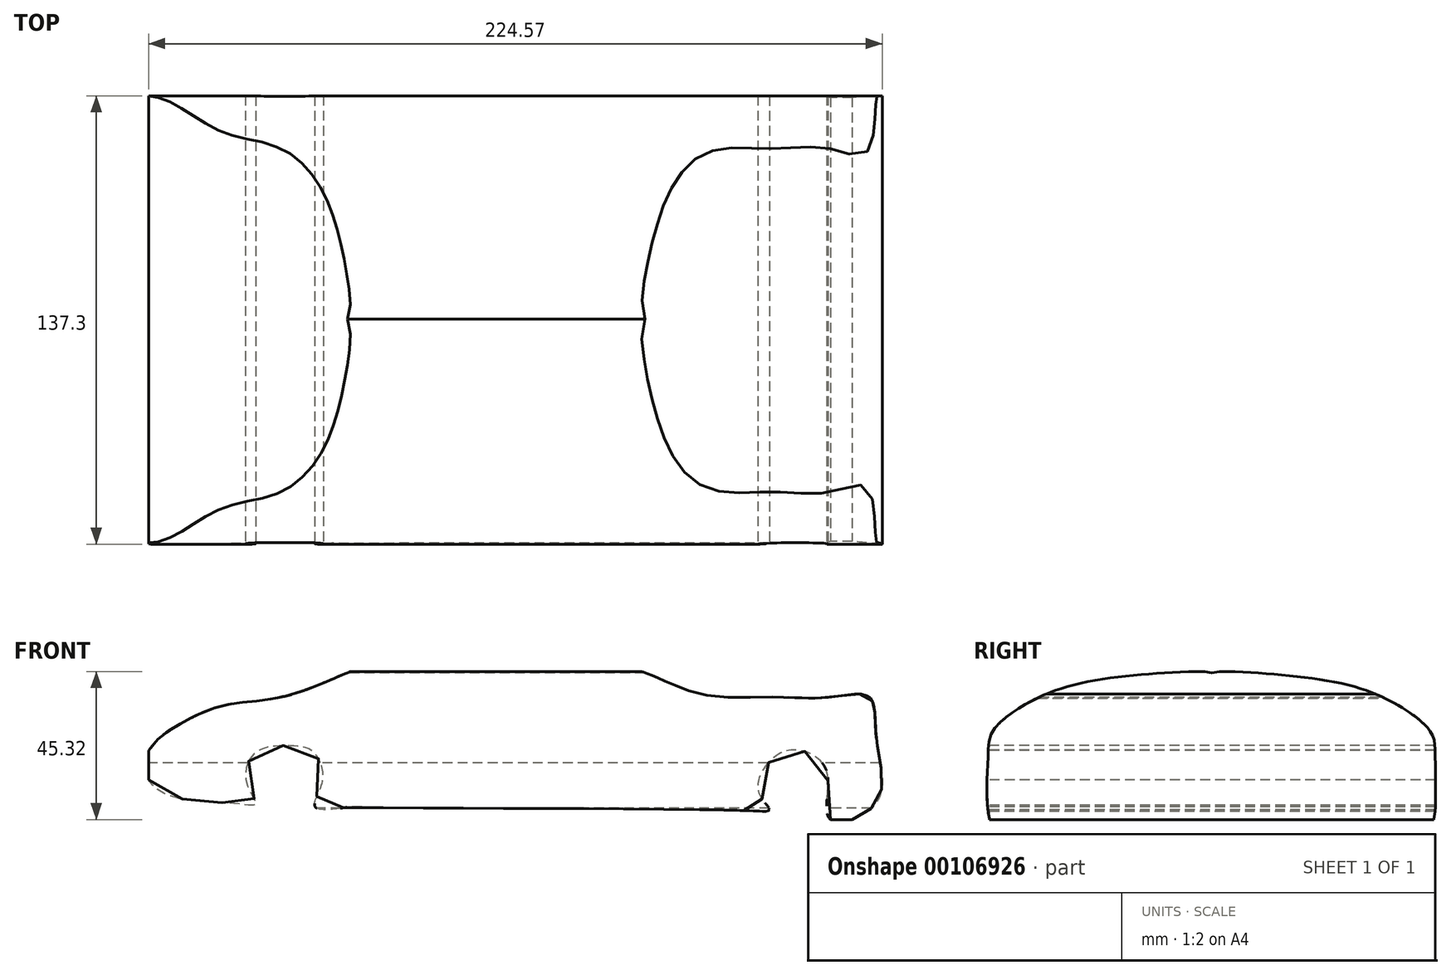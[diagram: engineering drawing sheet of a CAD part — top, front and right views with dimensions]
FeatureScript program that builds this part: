
annotation { "Feature Type Name" : "Feature", "Feature Type Description" : "" }
export const myFeature = defineFeature(function(context is Context, id is Id, definition is map)
    precondition{}
    {
        {
            var Q0;
            Q0=qCreatedBy(makeId("Top.planeOp"),FACE);
            var sketch = newSketch(context, id + "F0", { "sketchPlane" : qUnion([Q0])});
            skLineSegment(sketch, "E0.bottom", {"start": v(0, 0) * mm, "end": v(254, 0) * mm});
            skLineSegment(sketch, "E0.top", {"start": v(0, 144.86) * mm, "end": v(254, 144.86) * mm});
            skLineSegment(sketch, "E0.left", {"start": v(0, 0) * mm, "end": v(0, 144.86) * mm});
            skLineSegment(sketch, "E0.right", {"start": v(254, 0) * mm, "end": v(254, 144.86) * mm});
            skSolve(sketch);
        }
        {
            var Q0;
            Q0 = qSketchRegion(id + "F0", true);
            extrude(context, id + "F1", {"entities" : qUnion([Q0]), "depth" : 101.6 * mm});
        }
        {
            var Q0;
            Q0=makeQuery(id+"F1.opExtrude","SWEPT_FACE",FACE,{"disambiguationData":[OSD([sQuery(id+"F0.wireOp",EDGE,"E0.bottom")])]});
            var sketch = newSketch(context, id + "F2", { "sketchPlane" : qUnion([Q0])});
            skFitSpline(sketch, "E1", {"points": [v(0, 12.18) * mm, v(0, 21.15) * mm, v(9.08, 28.95) * mm, v(18.53, 33.57) * mm, v(27.34, 35.67) * mm, v(44.14, 38.4) * mm, v(75.47, 50.03) * mm, v(116.44, 51.7) * mm, v(150.3, 45.54) * mm, v(169.75, 38.24) * mm, v(191.08, 37.5) * mm, v(209.03, 37.5) * mm, v(220.63, 37.5) * mm, v(222.78, 24.47) * mm, v(222.78, 5.24) * mm, v(208.7, 0) * mm, v(207.8, 13.73) * mm, v(200.42, 20.98) * mm, v(191.6, 19.16) * mm, v(186.57, 8.99) * mm, v(190.07, 3.24) * mm, v(182.58, 2.74) * mm, v(67.47, 3.74) * mm, v(60.72, 3.74) * mm, v(51.08, 3.78) * mm, v(53.33, 12.02) * mm, v(50.33, 20.76) * mm, v(45.34, 22.51) * mm, v(37.1, 22.26) * mm, v(32.85, 20.51) * mm, v(30.34, 17.21) * mm, v(30.35, 10.03) * mm, v(32.85, 4.79) * mm, v(27.6, 4.78) * mm, v(9.73, 6.36) * mm, v(0, 12.18) * mm]});
            skLineSegment(sketch, "E2.bottom", {"start": v(-17.68, 122.97) * mm, "end": v(274.18, 122.97) * mm});
            skLineSegment(sketch, "E2.top", {"start": v(-17.68, -31.42) * mm, "end": v(274.18, -31.42) * mm});
            skLineSegment(sketch, "E2.left", {"start": v(-17.68, 122.97) * mm, "end": v(-17.68, -31.42) * mm});
            skLineSegment(sketch, "E2.right", {"start": v(274.18, 122.97) * mm, "end": v(274.18, -31.42) * mm});
            skSolve(sketch);
        }
        {
            var Q0;
            Q0 = qSketchRegion(id + "F2", true);
            extrude(context, id + "F3", {"entities" : qUnion([Q0]), "operationType" : NewBodyOperationType.REMOVE, "oppositeDirection" : true, "depth" : 207.71 * mm});
        }
        {
            var Q0;
            Q0=qCreatedBy(makeId("Right.planeOp"),FACE);
            var sketch = newSketch(context, id + "F4", { "sketchPlane" : qUnion([Q0])});
            skFitSpline(sketch, "E3", {"points": [v(76.44, 44.94) * mm, v(52.42, 44.13) * mm, v(25.18, 38.2) * mm, v(9.43, 27.2) * mm, v(7.9, 18.35) * mm, v(16.24, -12.88) * mm, v(75.87, -13.16) * mm, v(76.3, -4.94) * mm, v(76.43, 43.09) * mm, v(76.44, 44.94) * mm]});
            skLineSegment(sketch, "E4", {"start": v(76.44, 44.94) * mm, "end": v(76.3, -4.94) * mm});
            skFitSpline(sketch, "E5.MirrorCS", {"points": [v(76.44, 44.94) * mm, v(100.45, 44) * mm, v(127.67, 37.93) * mm, v(143.35, 26.85) * mm, v(144.83, 18) * mm, v(136.34, -13.2) * mm, v(76.7, -13.16) * mm, v(76.3, -4.94) * mm, v(76.44, 43.09) * mm, v(76.44, 44.94) * mm]});
            skLineSegment(sketch, "E6.bottom", {"start": v(179.45, 64.32) * mm, "end": v(-40.19, 64.32) * mm});
            skLineSegment(sketch, "E6.top", {"start": v(179.45, -40.14) * mm, "end": v(-40.19, -40.14) * mm});
            skLineSegment(sketch, "E6.left", {"start": v(179.45, 64.32) * mm, "end": v(179.45, -40.14) * mm});
            skLineSegment(sketch, "E6.right", {"start": v(-40.19, 64.32) * mm, "end": v(-40.19, -40.14) * mm});
            skSolve(sketch);
        }
        {
            var Q0;
            Q0 = qSketchRegion(id + "F4", true);
            extrude(context, id + "F5", {"entities" : qUnion([Q0]), "operationType" : NewBodyOperationType.REMOVE, "depth" : 260.3 * mm});
        }
    });
